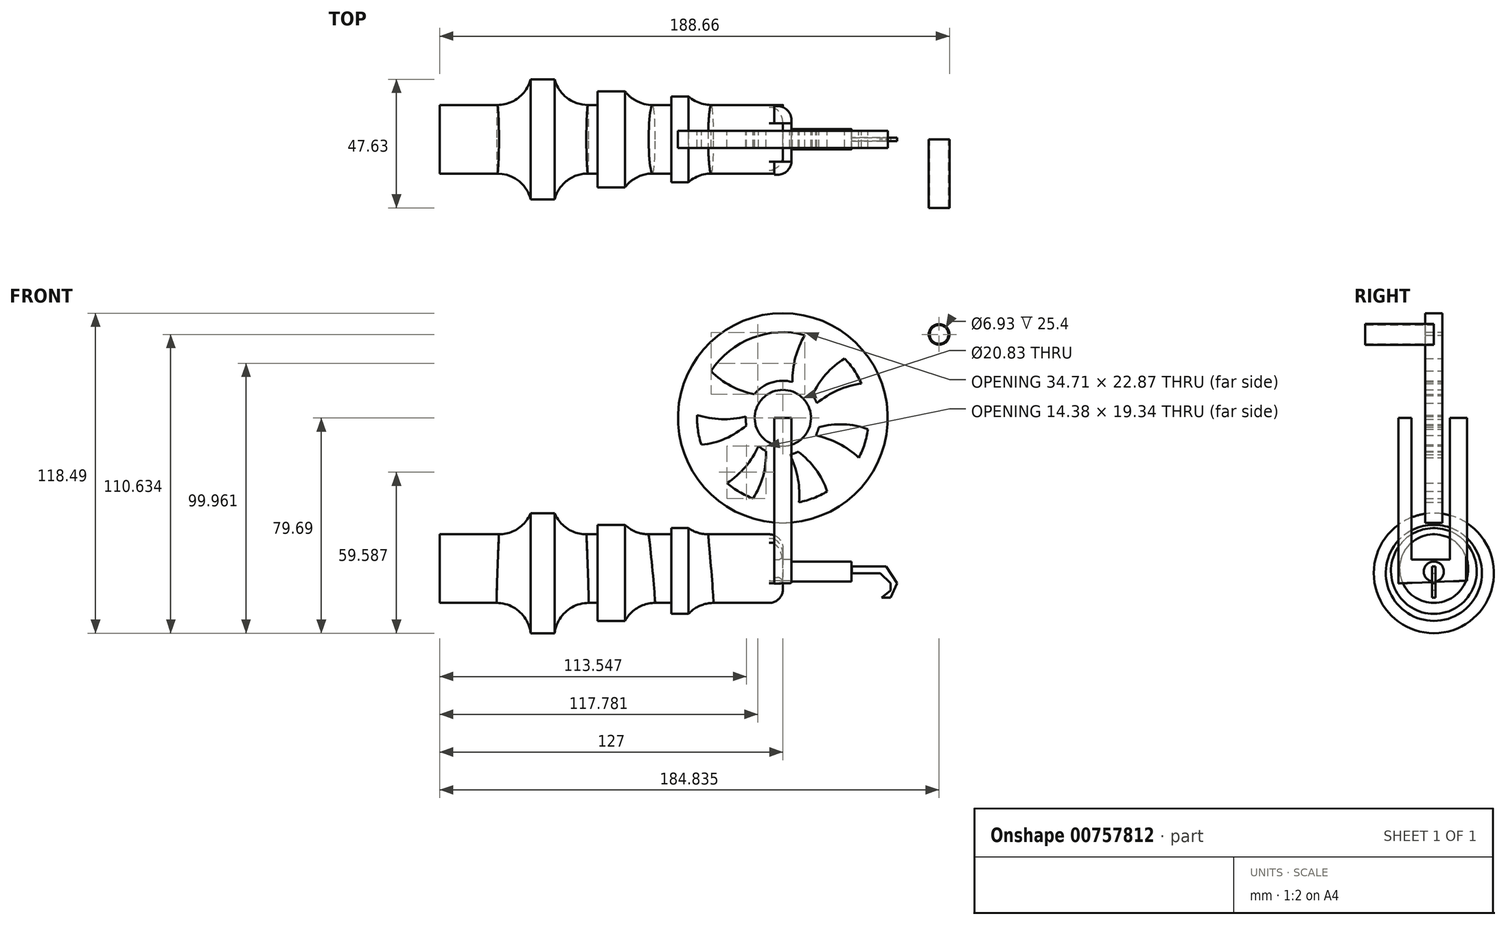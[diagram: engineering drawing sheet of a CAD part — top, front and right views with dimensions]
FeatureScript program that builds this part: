
annotation { "Feature Type Name" : "Feature", "Feature Type Description" : "" }
export const myFeature = defineFeature(function(context is Context, id is Id, definition is map)
    precondition{}
    {
        {
            var Q0;
            Q0=qCreatedBy(makeId("Front.planeOp"),FACE);
            var sketch = newSketch(context, id + "F0", { "sketchPlane" : qUnion([Q0])});
            skCircle(sketch, "E0", {"center": v(0, 0) * mm, "radius": 10.41 * mm});
            skArc(sketch, "E1", {"start": v(-1.85, 2.93) * mm, "mid": v(-2.94, 1.83) * mm, "end": v(-3.45, 0.38) * mm});
            skCircle(sketch, "E2", {"center": v(0, 0) * mm, "radius": 38.8 * mm});
            skArc(sketch, "E3", {"start": v(-5.15, 9.05) * mm, "mid": v(-5.63, 9.34) * mm, "end": v(-6.1, 9.64) * mm});
            skArc(sketch, "E4.1.1", {"start": v(3.58, 13.3) * mm, "mid": v(5.8, 25.9) * mm, "end": v(12.69, 36.67) * mm});
            skArc(sketch, "E4.2.1", {"start": v(12.63, 5.5) * mm, "mid": v(23.86, 11.61) * mm, "end": v(36.58, 12.94) * mm});
            skArc(sketch, "E4.3.1", {"start": v(12.17, -6.45) * mm, "mid": v(23.96, -11.41) * mm, "end": v(32.93, -20.53) * mm});
            skArc(sketch, "E4.4.1", {"start": v(2.55, -13.54) * mm, "mid": v(6.01, -25.85) * mm, "end": v(4.48, -38.54) * mm});
            skArc(sketch, "E4.5.1", {"start": v(-9, -10.43) * mm, "mid": v(-16.46, -20.82) * mm, "end": v(-27.34, -27.53) * mm});
            skArc(sketch, "E4.6.1", {"start": v(-10.29, 1.62) * mm, "mid": v(-10.82, 1.42) * mm, "end": v(-11.35, 1.24) * mm});
            skLineSegment(sketch, "E4.anchor1", {"start": v(0, 0) * mm, "end": v(-6.1, 9.64) * mm, "construction": true});
            skLineSegment(sketch, "E4.anchor2", {"start": v(0, 0) * mm, "end": v(-3.45, 0.38) * mm, "construction": true});
            skArc(sketch, "E5", {"start": v(0.32, 13.77) * mm, "mid": v(-3.15, 26.11) * mm, "end": v(-1.18, 38.78) * mm});
            skArc(sketch, "E6.1.0", {"start": v(-10.57, 8.84) * mm, "mid": v(-22.38, 13.82) * mm, "end": v(-31.06, 23.26) * mm});
            skArc(sketch, "E6.2.0", {"start": v(-13.5, -2.75) * mm, "mid": v(-24.76, -8.89) * mm, "end": v(-37.55, -9.79) * mm});
            skArc(sketch, "E6.3.0", {"start": v(-6.26, -12.27) * mm, "mid": v(-8.49, -24.9) * mm, "end": v(-15.76, -35.46) * mm});
            skArc(sketch, "E6.4.0", {"start": v(5.69, -12.55) * mm, "mid": v(14.17, -22.16) * mm, "end": v(17.9, -34.43) * mm});
            skArc(sketch, "E6.5.0", {"start": v(13.35, -3.38) * mm, "mid": v(26.16, -2.74) * mm, "end": v(38.08, -7.48) * mm});
            skArc(sketch, "E6.6.0", {"start": v(10.97, 8.33) * mm, "mid": v(18.45, 18.75) * mm, "end": v(29.58, 25.1) * mm});
            skCircle(sketch, "E7", {"center": v(0, 0) * mm, "radius": 31.75 * mm});
            skLineSegment(sketch, "E8.trimOffspring", {"start": v(-10.35, 1.13) * mm, "end": v(-11.35, 1.24) * mm, "construction": true});
            skCircle(sketch, "E9", {"center": v(0, 0) * mm, "radius": 13.78 * mm});
            skPoint(sketch, "E10.orphan", {"position": v(9.53, 4.2) * mm});
            skPoint(sketch, "E11.orphan", {"position": v(9.97, 3) * mm});
            skPoint(sketch, "E12.orphan", {"position": v(8.57, -5.92) * mm});
            skPoint(sketch, "E13.orphan", {"position": v(9.23, -4.82) * mm});
            skPoint(sketch, "E14.orphan", {"position": v(1.98, -10.22) * mm});
            skPoint(sketch, "E15.orphan", {"position": v(0.71, -10.39) * mm});
            skPoint(sketch, "E16.orphan", {"position": v(-6.76, -7.93) * mm});
            skPoint(sketch, "E17.orphan", {"position": v(-7.68, -7.04) * mm});
            skPoint(sketch, "E18.orphan", {"position": v(-10.4, 0.34) * mm});
            skArc(sketch, "E19.trimOffspring", {"start": v(-13.76, 0.53) * mm, "mid": v(-26.54, -0.11) * mm, "end": v(-38.57, 4.21) * mm});
            skPoint(sketch, "E20.orphan", {"position": v(-6.22, 8.35) * mm});
            skArc(sketch, "E21.trimOffspring", {"start": v(-8.17, 11.1) * mm, "mid": v(-16.63, 20.68) * mm, "end": v(-20.76, 32.78) * mm});
            skPoint(sketch, "E22.orphan", {"position": v(2.65, 10.07) * mm});
            skPoint(sketch, "E23.orphan", {"position": v(3.86, 9.67) * mm});
            skSolve(sketch);
        }
        {
            var Q0;
            Q0 = qSketchRegion(id + "F0", true);
            var Q1;
            {var subQ0=sQuery(id+"F0.wireOp",EDGE,"E4.1.1");Q1=makeQuery(id+"F0.imprint","IMPRINT",FACE,{"disambiguationData":[TD([[makeQuery(id+"F0.imprint","IMPRINT",EDGE,{"derivedFrom":subQ0}),1.0]])]});}
            var Q2;
            {var subQ0=sQuery(id+"F0.wireOp",EDGE,"E4.2.1");Q2=makeQuery(id+"F0.imprint","IMPRINT",FACE,{"disambiguationData":[TD([[makeQuery(id+"F0.imprint","IMPRINT",EDGE,{"derivedFrom":subQ0}),1.0]])]});}
            var Q3;
            {var subQ0=sQuery(id+"F0.wireOp",EDGE,"E4.3.1");Q3=makeQuery(id+"F0.imprint","IMPRINT",FACE,{"disambiguationData":[TD([[makeQuery(id+"F0.imprint","IMPRINT",EDGE,{"derivedFrom":subQ0}),1.0]])]});}
            var Q4;
            {var subQ0=sQuery(id+"F0.wireOp",EDGE,"E4.4.1");Q4=makeQuery(id+"F0.imprint","IMPRINT",FACE,{"disambiguationData":[TD([[makeQuery(id+"F0.imprint","IMPRINT",EDGE,{"derivedFrom":subQ0}),1.0]])]});}
            var Q5;
            {var subQ0=sQuery(id+"F0.wireOp",EDGE,"E4.5.1");Q5=makeQuery(id+"F0.imprint","IMPRINT",FACE,{"disambiguationData":[TD([[makeQuery(id+"F0.imprint","IMPRINT",EDGE,{"derivedFrom":subQ0}),1.0]])]});}
            var Q6;
            {var subQ0=sQuery(id+"F0.wireOp",EDGE,"E6.2.0");Q6=makeQuery(id+"F0.imprint","IMPRINT",FACE,{"disambiguationData":[TD([[makeQuery(id+"F0.imprint","IMPRINT",EDGE,{"derivedFrom":subQ0}),-1.0]])]});}
            var Q7;
            {var subQ0=sQuery(id+"F0.wireOp",EDGE,"E6.1.0");Q7=makeQuery(id+"F0.imprint","IMPRINT",FACE,{"disambiguationData":[TD([[makeQuery(id+"F0.imprint","IMPRINT",EDGE,{"derivedFrom":subQ0}),-1.0]])]});}
            var Q8;
            {var subQ8=sQuery(id+"F0.wireOp",EDGE,"E0");var subQ9=makeQuery(id+"F0.imprint","IMPRINT",VERTEX,{"disambiguationData":[OD(0.0)],"derivedFrom":subQ8});Q8=makeQuery(id+"F0.imprint","IMPRINT",FACE,{"disambiguationData":[TD([[makeQuery(id+"F0.imprint","IMPRINT",EDGE,{"disambiguationData":[TD([[subQ9,-1.0]])],"derivedFrom":subQ8}),-1.0]])]});}
            var Q9;
            Q9=makeQuery(id+"F0.imprint","IMPRINT",FACE,{"disambiguationData":[TD([[makeQuery(id+"F0.imprint","IMPRINT",EDGE,{"derivedFrom":sQuery(id+"F0.wireOp",EDGE,"539e0326-62d8-41c1-9314-10fc468e663a")}),1.0]])]});
            extrude(context, id + "F1", {"entities" : qUnion([Q0, Q1, Q2, Q3, Q4, Q5, Q6, Q7, Q8, Q9]), "endBound" : BoundingType.SYMMETRIC, "depth" : 6.35 * mm, "offsetDistance" : 25.4 * mm});
        }
        {
            var Q0;
            Q0=qCreatedBy(makeId("Right.planeOp"),FACE);
            var sketch = newSketch(context, id + "F2", { "sketchPlane" : qUnion([Q0])});
            skPoint(sketch, "E24.start.orphan", {"position": v(-13.13, 0) * mm});
            skPoint(sketch, "E25.start.orphan", {"position": v(12.27, 0) * mm});
            skLineSegment(sketch, "E26", {"start": v(12.27, 0) * mm, "end": v(12.27, -60.25) * mm});
            skLineSegment(sketch, "E27", {"start": v(-13.13, 0) * mm, "end": v(-13.13, -61.26) * mm});
            skLineSegment(sketch, "E28", {"start": v(-13.13, -61.26) * mm, "end": v(12.27, -60.25) * mm});
            skLineSegment(sketch, "E29", {"start": v(-13.13, 0) * mm, "end": v(-8.3, 0) * mm});
            skLineSegment(sketch, "E30", {"start": v(-8.3, 0) * mm, "end": v(-8.3, -52.45) * mm});
            skLineSegment(sketch, "E31", {"start": v(-8.3, -52.45) * mm, "end": v(5.9, -52.45) * mm});
            skLineSegment(sketch, "E32", {"start": v(5.9, -52.45) * mm, "end": v(5.9, 0) * mm});
            skLineSegment(sketch, "E33", {"start": v(12.27, 0) * mm, "end": v(5.9, 0) * mm});
            skSolve(sketch);
        }
        {
            var Q0;
            Q0 = qSketchRegion(id + "F2", true);
            extrude(context, id + "F3", {"entities" : qUnion([Q0]), "endBound" : BoundingType.SYMMETRIC, "depth" : 6.35 * mm, "offsetDistance" : 25.4 * mm});
        }
        {
            var Q0;
            Q0=qCreatedBy(makeId("Right.planeOp"),FACE);
            var sketch = newSketch(context, id + "F4", { "sketchPlane" : qUnion([Q0])});
            skCircle(sketch, "E34", {"center": v(0, -55.77) * mm, "radius": 12.7 * mm});
            skSolve(sketch);
        }
        {
            var Q0;
            Q0 = qSketchRegion(id + "F4", true);
            extrude(context, id + "F5", {"entities" : qUnion([Q0]), "operationType" : NewBodyOperationType.ADD, "oppositeDirection" : true, "depth" : 127 * mm, "offsetDistance" : 25.4 * mm});
        }
        {
            var Q0;
            Q0=qCreatedBy(makeId("Right.planeOp"),FACE);
            cPlane(context, id + "F6", {"entities" : qUnion([Q0]), "cplaneType" : CPlaneType.OFFSET, "offset" : 38.1 * mm, "oppositeDirection" : true, "width" : 152.4 * mm, "height" : 152.4 * mm});
        }
        {
            var Q0;
            Q0=qCreatedBy(id+"F6.planeOp",FACE);
            var sketch = newSketch(context, id + "F7", { "sketchPlane" : qUnion([Q0])});
            skCircle(sketch, "E35", {"center": v(0, -56.66) * mm, "radius": 15.88 * mm});
            skSolve(sketch);
        }
        {
            var Q0;
            Q0=qCreatedBy(id+"F6.planeOp",FACE);
            cPlane(context, id + "F8", {"entities" : qUnion([Q0]), "cplaneType" : CPlaneType.OFFSET, "offset" : 25.4 * mm, "oppositeDirection" : true, "width" : 152.4 * mm, "height" : 152.4 * mm});
        }
        {
            var Q0;
            Q0=qCreatedBy(id+"F8.planeOp",FACE);
            var sketch = newSketch(context, id + "F9", { "sketchPlane" : qUnion([Q0])});
            skCircle(sketch, "E36", {"center": v(0, -57.35) * mm, "radius": 17.78 * mm});
            skSolve(sketch);
        }
        {
            var Q0;
            Q0=qCreatedBy(id+"F8.planeOp",FACE);
            cPlane(context, id + "F10", {"entities" : qUnion([Q0]), "cplaneType" : CPlaneType.OFFSET, "offset" : 25.4 * mm, "oppositeDirection" : true, "width" : 152.4 * mm, "height" : 152.4 * mm});
        }
        {
            var Q0;
            Q0=qCreatedBy(id+"F10.planeOp",FACE);
            var sketch = newSketch(context, id + "F11", { "sketchPlane" : qUnion([Q0])});
            skCircle(sketch, "E37", {"center": v(0, -57.47) * mm, "radius": 22.23 * mm});
            skSolve(sketch);
        }
        {
            var Q0;
            Q0=qCreatedBy(makeId("Right.planeOp"),FACE);
            var sketch = newSketch(context, id + "F12", { "sketchPlane" : qUnion([Q0])});
            skCircle(sketch, "E38", {"center": v(0, -56.85) * mm, "radius": 3.72 * mm});
            skSolve(sketch);
        }
        {
            var Q0;
            Q0 = qSketchRegion(id + "F12", true);
            extrude(context, id + "F13", {"entities" : qUnion([Q0]), "operationType" : NewBodyOperationType.ADD, "depth" : 25.4 * mm, "offsetDistance" : 25.4 * mm});
        }
        {
            var Q0;
            Q0=qCreatedBy(makeId("Front.planeOp"),FACE);
            var sketch = newSketch(context, id + "F14", { "sketchPlane" : qUnion([Q0])});
            skLineSegment(sketch, "E39", {"start": v(25.48, -54.99) * mm, "end": v(38.25, -54.99) * mm});
            skLineSegment(sketch, "E40", {"start": v(38.25, -54.99) * mm, "end": v(42.29, -61.2) * mm});
            skLineSegment(sketch, "E41", {"start": v(42.29, -61.2) * mm, "end": v(39.9, -66.47) * mm});
            skLineSegment(sketch, "E42", {"start": v(39.9, -66.47) * mm, "end": v(39.9, -61.16) * mm});
            skLineSegment(sketch, "E43", {"start": v(39.9, -61.16) * mm, "end": v(36.07, -57.52) * mm});
            skLineSegment(sketch, "E44", {"start": v(36.07, -57.52) * mm, "end": v(25.46, -57.52) * mm});
            skLineSegment(sketch, "E45", {"start": v(25.46, -57.52) * mm, "end": v(25.48, -54.99) * mm});
            skSolve(sketch);
        }
        {
            var Q0;
            Q0=makeQuery(id+"F14.imprint","IMPRINT",FACE,{"disambiguationData":[TD([[makeQuery(id+"F14.imprint","IMPRINT",EDGE,{"derivedFrom":sQuery(id+"F14.wireOp",EDGE,"E39")}),-1.0]])]});
            extrude(context, id + "F15", {"entities" : qUnion([Q0]), "endBound" : BoundingType.SYMMETRIC, "depth" : 1.27 * mm, "offsetDistance" : 25.4 * mm});
        }
        {
            var Q0;
            Q0=makeQuery(id+"F11.imprint","IMPRINT",FACE,{"disambiguationData":[TD([[makeQuery(id+"F11.imprint","IMPRINT",EDGE,{"derivedFrom":sQuery(id+"F11.wireOp",EDGE,"E37")}),1.0]])]});
            extrude(context, id + "F16", {"entities" : qUnion([Q0]), "operationType" : NewBodyOperationType.ADD, "endBound" : BoundingType.SYMMETRIC, "depth" : 8.9 * mm, "offsetDistance" : 25.4 * mm});
        }
        {
            var Q0;
            Q0=makeQuery(id+"F9.imprint","IMPRINT",FACE,{"disambiguationData":[TD([[makeQuery(id+"F9.imprint","IMPRINT",EDGE,{"derivedFrom":sQuery(id+"F9.wireOp",EDGE,"E36")}),1.0]])]});
            extrude(context, id + "F17", {"entities" : qUnion([Q0]), "operationType" : NewBodyOperationType.ADD, "endBound" : BoundingType.SYMMETRIC, "depth" : 10.16 * mm, "offsetDistance" : 25.4 * mm});
        }
        {
            var Q0;
            Q0=makeQuery(id+"F7.imprint","IMPRINT",FACE,{"disambiguationData":[TD([[makeQuery(id+"F7.imprint","IMPRINT",EDGE,{"derivedFrom":sQuery(id+"F7.wireOp",EDGE,"E35")}),1.0]])]});
            extrude(context, id + "F18", {"entities" : qUnion([Q0]), "operationType" : NewBodyOperationType.ADD, "endBound" : BoundingType.SYMMETRIC, "depth" : 6.35 * mm, "offsetDistance" : 25.4 * mm});
        }
        {
            var Q0;
            {var subQ3=sQuery(id+"F2.wireOp",EDGE,"E26");var subQ4=sQuery(id+"F4.wireOp",EDGE,"E34");Q0=makeQuery(id+"F17.boolean.opBoolean","INTERSECT",EDGE,{"derivedFrom":[makeQuery(id+"F16.boolean.opBoolean","SPLIT",FACE,{"disambiguationData":[TD([makeQuery(id+"F3.opExtrude","SWEPT_FACE",FACE,{"disambiguationData":[OSD([subQ3])]})])],"derivedFrom":makeQuery(id+"F5.opExtrude","SWEPT_FACE",FACE,{"disambiguationData":[OSD([subQ4])]})}),makeQuery(id+"F17.opExtrude","CAP_FACE",FACE,{"disambiguationData":[OSD([sQuery(id+"F9.wireOp",EDGE,"E36")])],"isStart":false})]});}
            var Q1;
            {var subQ5=sQuery(id+"F2.wireOp",EDGE,"E26");var subQ7=makeQuery(id+"F3.opExtrude","SWEPT_FACE",FACE,{"disambiguationData":[OSD([subQ5])]});var subQ9=sQuery(id+"F4.wireOp",EDGE,"E34");Q1=makeQuery(id+"F18.boolean.opBoolean","INTERSECT",EDGE,{"derivedFrom":[makeQuery(id+"F17.boolean.opBoolean","SPLIT",FACE,{"disambiguationData":[TD([subQ7])],"derivedFrom":makeQuery(id+"F16.boolean.opBoolean","SPLIT",FACE,{"disambiguationData":[TD([subQ7])],"derivedFrom":makeQuery(id+"F5.opExtrude","SWEPT_FACE",FACE,{"disambiguationData":[OSD([subQ9])]})})}),makeQuery(id+"F18.opExtrude","CAP_FACE",FACE,{"disambiguationData":[OSD([sQuery(id+"F7.wireOp",EDGE,"E35")])],"isStart":false})]});}
            var Q2;
            Q2=makeQuery(id+"F16.boolean.opBoolean","INTERSECT",EDGE,{"derivedFrom":[makeQuery(id+"F5.opExtrude","SWEPT_FACE",FACE,{"disambiguationData":[OSD([sQuery(id+"F4.wireOp",EDGE,"E34")])]}),makeQuery(id+"F16.opExtrude","CAP_FACE",FACE,{"disambiguationData":[OSD([sQuery(id+"F11.wireOp",EDGE,"E37")])],"isStart":false})]});
            var Q3;
            Q3=makeQuery(id+"F16.boolean.opBoolean","INTERSECT",EDGE,{"derivedFrom":[makeQuery(id+"F5.opExtrude","SWEPT_FACE",FACE,{"disambiguationData":[OSD([sQuery(id+"F4.wireOp",EDGE,"E34")])]}),makeQuery(id+"F16.opExtrude","CAP_FACE",FACE,{"disambiguationData":[OSD([sQuery(id+"F11.wireOp",EDGE,"E37")])],"isStart":true})]});
            fillet(context, id + "F19", {"entities" : qUnion([Q0, Q1, Q2, Q3]), "radius" : 12.7 * mm, "tangentPropagation" : true, "allowEdgeOverflow" : false});
        }
        {
            var Q0;
            {var subQ0=sQuery(id+"F4.wireOp",EDGE,"E34");Q0=makeQuery(id+"F5.boolean.opBoolean","SPLIT",EDGE,{"disambiguationData":[TD([makeQuery(id+"F3.opExtrude","SWEPT_FACE",FACE,{"disambiguationData":[OSD([sQuery(id+"F2.wireOp",EDGE,"E28")])]})])],"derivedFrom":makeQuery(id+"F5.opExtrude","CAP_EDGE",EDGE,{"disambiguationData":[OSD([subQ0])],"isStart":true})});}
            var Q1;
            {var subQ0=sQuery(id+"F4.wireOp",EDGE,"E34");Q1=makeQuery(id+"F5.boolean.opBoolean","SPLIT",EDGE,{"disambiguationData":[TD([makeQuery(id+"F3.opExtrude","SWEPT_FACE",FACE,{"disambiguationData":[OSD([sQuery(id+"F2.wireOp",EDGE,"E30")])]})])],"derivedFrom":makeQuery(id+"F5.opExtrude","CAP_EDGE",EDGE,{"disambiguationData":[OSD([subQ0])],"isStart":true})});}
            var Q2;
            Q2=makeQuery(id+"F3.opExtrude","CAP_EDGE",EDGE,{"disambiguationData":[OSD([sQuery(id+"F2.wireOp",EDGE,"E26")])],"isStart":false});
            var Q3;
            Q3=makeQuery(id+"F3.opExtrude","CAP_EDGE",EDGE,{"disambiguationData":[OSD([sQuery(id+"F2.wireOp",EDGE,"E27")])],"isStart":false});
            fillet(context, id + "F20", {"entities" : qUnion([Q0, Q1, Q2, Q3]), "radius" : 5.08 * mm, "tangentPropagation" : true, "allowEdgeOverflow" : false});
        }
        {
            var Q0;
            Q0=makeQuery(id+"F15.opExtrude","CAP_FACE",FACE,{"disambiguationData":[OSD([sQuery(id+"F14.wireOp",EDGE,"E39"),sQuery(id+"F14.wireOp",EDGE,"E40"),sQuery(id+"F14.wireOp",EDGE,"E41"),sQuery(id+"F14.wireOp",EDGE,"E42"),sQuery(id+"F14.wireOp",EDGE,"E43"),sQuery(id+"F14.wireOp",EDGE,"E44"),sQuery(id+"F14.wireOp",EDGE,"E45")])],"isStart":false});
            var sketch = newSketch(context, id + "F21", { "sketchPlane" : qUnion([Q0])});
            skLineSegment(sketch, "E46", {"start": v(39.9, -66.47) * mm, "end": v(36.53, -66.47) * mm});
            skLineSegment(sketch, "E47", {"start": v(36.53, -66.47) * mm, "end": v(39.9, -63.81) * mm});
            skSolve(sketch);
        }
        {
            var Q0;
            {var subQ0=sQuery(id+"F21.wireOp",EDGE,"E46");Q0=makeQuery(id+"F21.imprint","IMPRINT",FACE,{"disambiguationData":[TD([[makeQuery(id+"F21.imprint","IMPRINT",EDGE,{"derivedFrom":subQ0}),-1.0]])]});}
            var sketch = newSketch(context, id + "F22", { "sketchPlane" : qUnion([Q0])});
            skSolve(sketch);
        }
        {
            var Q0;
            {var subQ0=sQuery(id+"F21.wireOp",EDGE,"E46");Q0=makeQuery(id+"F22.imprint","IMPRINT",FACE,{"disambiguationData":[TD([[makeQuery(id+"F22.imprint","IMPRINT",EDGE,{"derivedFrom":makeQuery(id+"F21.imprint","IMPRINT",EDGE,{"derivedFrom":subQ0})}),-1.0]])]});}
            extrude(context, id + "F23", {"entities" : qUnion([Q0]), "operationType" : NewBodyOperationType.ADD, "oppositeDirection" : true, "depth" : 1.27 * mm, "offsetDistance" : 25.4 * mm});
        }
        {
            var Q0;
            Q0=qCreatedBy(makeId("Front.planeOp"),FACE);
            var sketch = newSketch(context, id + "F24", { "sketchPlane" : qUnion([Q0])});
            skCircle(sketch, "E48", {"center": v(57.84, 30.94) * mm, "radius": 3.82 * mm});
            skCircle(sketch, "E49", {"center": v(57.84, 30.94) * mm, "radius": 3.47 * mm});
            skSolve(sketch);
        }
        {
            var Q0;
            Q0=makeQuery(id+"F24.imprint","IMPRINT",FACE,{"disambiguationData":[TD([[makeQuery(id+"F24.imprint","IMPRINT",EDGE,{"derivedFrom":sQuery(id+"F24.wireOp",EDGE,"E48")}),1.0]])]});
            extrude(context, id + "F25", {"entities" : qUnion([Q0]), "depth" : 25.4 * mm, "offsetDistance" : 25.4 * mm});
        }
        {
            var Q0;
            Q0 = qSketchRegion(id + "F24", true);
            extrude(context, id + "F26", {"entities" : qUnion([Q0]), "operationType" : NewBodyOperationType.ADD, "depth" : 25.4 * mm, "offsetDistance" : 25.4 * mm});
        }
    });
